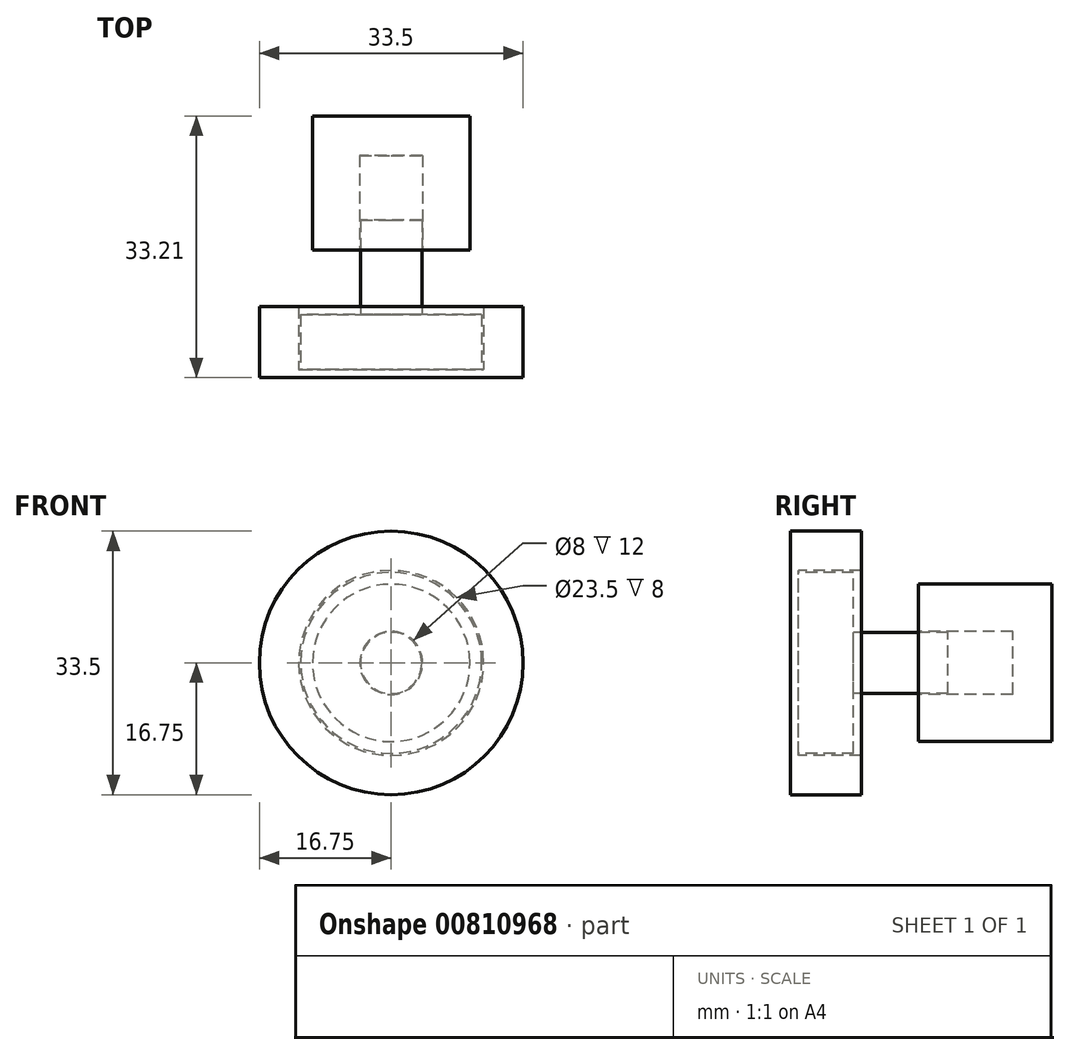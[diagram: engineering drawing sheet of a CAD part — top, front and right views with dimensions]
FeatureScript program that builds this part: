
annotation { "Feature Type Name" : "Feature", "Feature Type Description" : "" }
export const myFeature = defineFeature(function(context is Context, id is Id, definition is map)
    precondition{}
    {
        {
            var Q0;
            Q0=qCreatedBy(makeId("Top.planeOp"),FACE);
            var sketch = newSketch(context, id + "F0", { "sketchPlane" : qUnion([Q0])});
            skLineSegment(sketch, "E0", {"start": v(0, 0) * mm, "end": v(0, 20) * mm});
            skLineSegment(sketch, "E1", {"start": v(0, 20) * mm, "end": v(3.9, 20) * mm});
            skLineSegment(sketch, "E2", {"start": v(3.9, 20) * mm, "end": v(3.9, 1) * mm});
            skLineSegment(sketch, "E3", {"start": v(3.9, 1) * mm, "end": v(11.75, 1) * mm});
            skLineSegment(sketch, "E4", {"start": v(0, 0) * mm, "end": v(16.75, 0) * mm});
            skLineSegment(sketch, "E5", {"start": v(16.75, 0) * mm, "end": v(16.75, 9) * mm});
            skLineSegment(sketch, "E6", {"start": v(11.75, 1) * mm, "end": v(11.75, 9) * mm});
            skLineSegment(sketch, "E7", {"start": v(11.75, 9) * mm, "end": v(16.75, 9) * mm});
            skSolve(sketch);
        }
        {
            var Q0;
            Q0=makeQuery(id+"F0.imprint","IMPRINT",FACE,{"disambiguationData":[TD([[makeQuery(id+"F0.imprint","IMPRINT",EDGE,{"derivedFrom":sQuery(id+"F0.wireOp",EDGE,"E0")}),-1.0]])]});
            var Q1;
            Q1 = qSketchRegion(id + "F2", true);
            var Q2;
            Q2=sQuery(id+"F0.wireOp",EDGE,"E0");
            revolve(context, id + "F1", {"surfaceOperationType" : NewSurfaceOperationType.NEW, "entities" : qUnion([Q0, Q1]), "axis" : qUnion([Q2]), "revolveType" : RevolveType.FULL});
        }
        {
            var Q0;
            Q0=qCreatedBy(makeId("Top.planeOp"),FACE);
            var sketch = newSketch(context, id + "F2", { "sketchPlane" : qUnion([Q0])});
            skLineSegment(sketch, "E8", {"start": v(-4, 16.21) * mm, "end": v(-4, 28.21) * mm});
            skLineSegment(sketch, "E9", {"start": v(-4, 28.21) * mm, "end": v(0, 28.21) * mm});
            skLineSegment(sketch, "E10", {"start": v(0, 28.21) * mm, "end": v(0, 33.21) * mm});
            skLineSegment(sketch, "E11", {"start": v(-4, 16.21) * mm, "end": v(-10, 16.21) * mm});
            skLineSegment(sketch, "E12", {"start": v(-10, 16.21) * mm, "end": v(-10, 33.21) * mm});
            skLineSegment(sketch, "E13", {"start": v(-10, 33.21) * mm, "end": v(0, 33.21) * mm});
            skSolve(sketch);
        }
        {
            var Q0;
            Q0=makeQuery(id+"F2.imprint","IMPRINT",FACE,{"disambiguationData":[TD([[makeQuery(id+"F2.imprint","IMPRINT",EDGE,{"derivedFrom":sQuery(id+"F2.wireOp",EDGE,"E8")}),1.0]])]});
            var Q1;
            Q1=sQuery(id+"F2.wireOp",EDGE,"E9");
            var Q2;
            Q2=sQuery(id+"F2.wireOp",EDGE,"E11");
            var Q3;
            Q3=sQuery(id+"F2.wireOp",EDGE,"E8");
            var Q4;
            Q4=sQuery(id+"F2.wireOp",EDGE,"E12");
            var Q5;
            Q5=sQuery(id+"F2.wireOp",EDGE,"E10");
            revolve(context, id + "F3", {"surfaceOperationType" : NewSurfaceOperationType.NEW, "entities" : qUnion([Q0]), "surfaceEntities" : qUnion([Q1, Q2, Q3, Q4]), "axis" : qUnion([Q5]), "revolveType" : RevolveType.FULL});
        }
        {
            var Q0;
            Q0=qCreatedBy(makeId("Front.planeOp"),FACE);
            var sketch = newSketch(context, id + "F4", { "sketchPlane" : qUnion([Q0])});
            skCircle(sketch, "E14", {"center": v(0, 0) * mm, "radius": 11.5 * mm});
            skSolve(sketch);
        }
        {
            var Q0;
            Q0=makeQuery(id+"F4.imprint","IMPRINT",FACE,{"disambiguationData":[TD([[makeQuery(id+"F4.imprint","IMPRINT",EDGE,{"derivedFrom":sQuery(id+"F4.wireOp",EDGE,"E14")}),1.0]])]});
            extrude(context, id + "F5", {"entities" : qUnion([Q0]), "operationType" : NewBodyOperationType.ADD, "oppositeDirection" : true, "depth" : 8 * mm, "offsetDistance" : 25 * mm});
        }
    });
